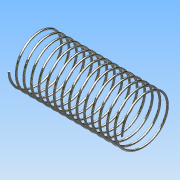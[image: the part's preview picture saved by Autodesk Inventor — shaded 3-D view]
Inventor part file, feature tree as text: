
AUTODESK INVENTOR PART (.ipt)
format: ipt  version: 2015 (Build 190159000, 159)  size: 401,408 bytes
history: native  units: in
note: dims shown in document units (in); Inventor stores cm internally (conversion verified against a paired STEP export)
features: sketch x2, extrude x1, helix x1
ambient origin geometry x8: Origin, YZ Plane, XZ Plane, XY Plane, X Axis, Y Axis, Z Axis, Center Point
bodies: Solid1 (feature_tree)
feature tree (4):
  extrude  "Extrusion1"  TaperAngle=0.0deg  [1 undecoded]
  helix  "Coil2"  [1 undecoded]
  sketch  "Sketch1"  dims[d0=0.67in d2=0.0in d12=0.025in]
  sketch  "Sketch3"  dims[d13=0.1in d14=1.5in d15=0.3937in d16=0.0in d17=90.0deg d18=90.0deg d19=0.0in d20=0.0in]
note: 2 required parameter values undecoded (feature->parameter linkage not recoverable at this tier; creation-order binding heuristic only, values carry confidence <= 0.55)
